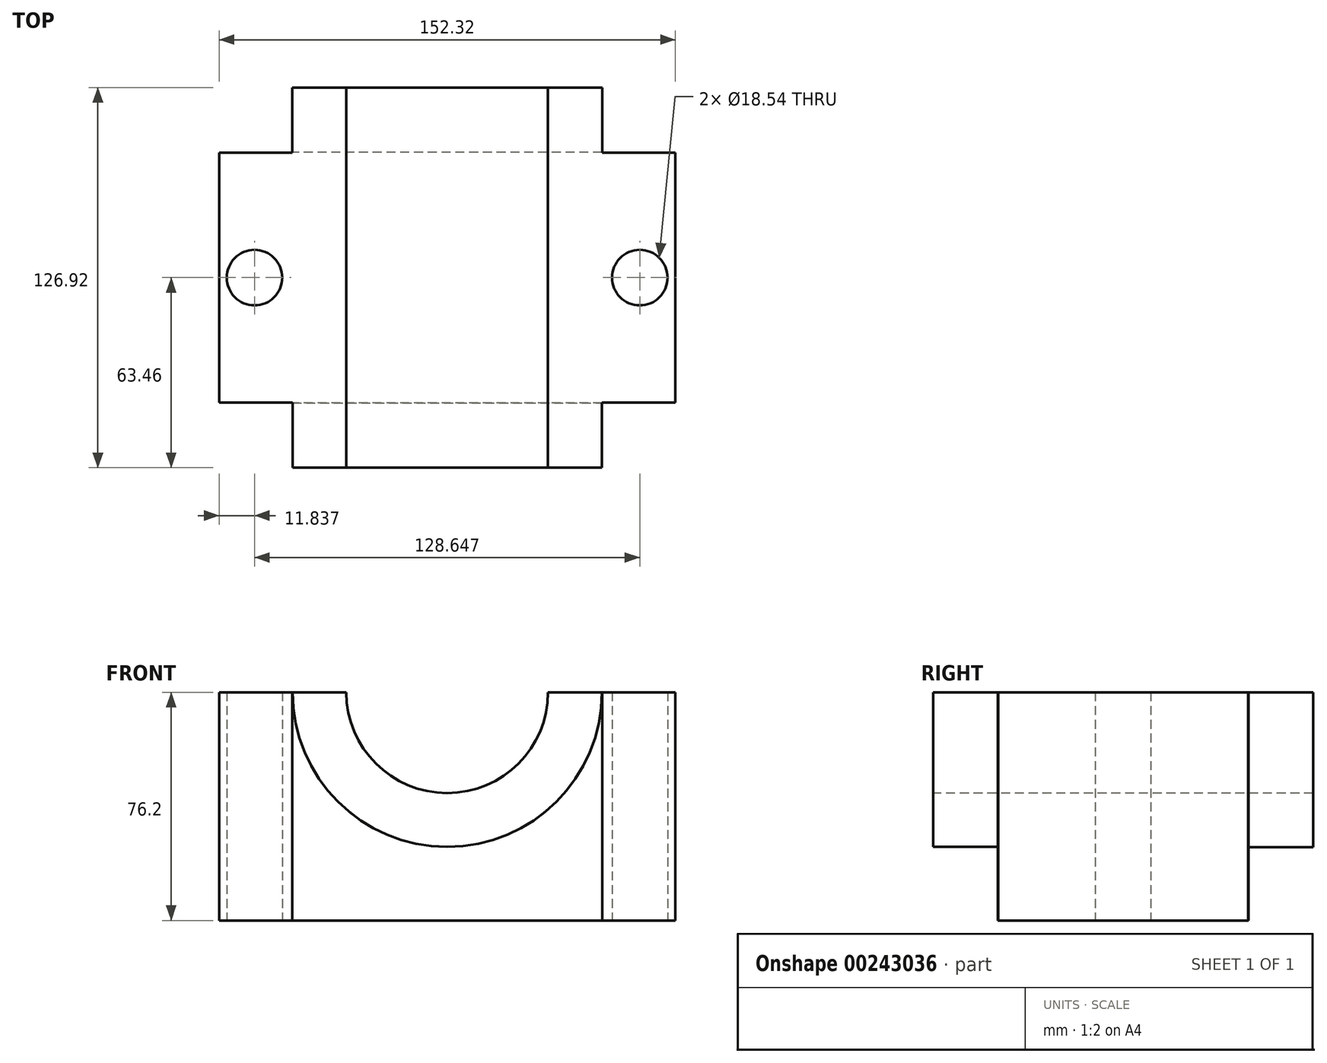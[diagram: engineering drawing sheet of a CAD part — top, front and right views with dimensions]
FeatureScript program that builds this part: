
annotation { "Feature Type Name" : "Feature", "Feature Type Description" : "" }
export const myFeature = defineFeature(function(context is Context, id is Id, definition is map)
    precondition{}
    {
        {
            var Q0;
            Q0=qCreatedBy(makeId("Top.planeOp"),FACE);
            var sketch = newSketch(context, id + "F0", { "sketchPlane" : qUnion([Q0])});
            skLineSegment(sketch, "E0.bottom", {"start": v(76.16, 41.7) * mm, "end": v(-76.16, 41.7) * mm});
            skLineSegment(sketch, "E0.top", {"start": v(76.16, -41.7) * mm, "end": v(-76.16, -41.7) * mm});
            skLineSegment(sketch, "E0.left", {"start": v(76.16, 41.7) * mm, "end": v(76.16, -41.7) * mm});
            skLineSegment(sketch, "E0.right", {"start": v(-76.16, 41.7) * mm, "end": v(-76.16, -41.7) * mm});
            skLineSegment(sketch, "E1.bottom", {"start": v(51.73, 63.46) * mm, "end": v(-51.73, 63.46) * mm});
            skLineSegment(sketch, "E1.top", {"start": v(51.73, -63.46) * mm, "end": v(-51.73, -63.46) * mm});
            skLineSegment(sketch, "E1.left", {"start": v(51.73, 63.46) * mm, "end": v(51.73, -63.46) * mm});
            skLineSegment(sketch, "E1.right", {"start": v(-51.73, 63.46) * mm, "end": v(-51.73, -63.46) * mm});
            skCircle(sketch, "E2", {"center": v(-64.32, 0) * mm, "radius": 9.27 * mm});
            skCircle(sketch, "E3", {"center": v(64.32, 0) * mm, "radius": 9.27 * mm});
            skSolve(sketch);
        }
        {
            var Q0;
            Q0 = qSketchRegion(id + "F0", true);
            extrude(context, id + "F1", {"entities" : qUnion([Q0]), "depth" : 76.2 * mm});
        }
        {
            var Q0;
            Q0=makeQuery(id+"F1.opExtrude","SWEPT_FACE",FACE,{"disambiguationData":[OSD([sQuery(id+"F0.wireOp",EDGE,"E1.top")])]});
            var sketch = newSketch(context, id + "F2", { "sketchPlane" : qUnion([Q0])});
            skArc(sketch, "E4", {"start": v(-51.65, 76.2) * mm, "mid": v(0, 24.55) * mm, "end": v(51.65, 76.2) * mm});
            skArc(sketch, "E5", {"start": v(-33.68, 76.2) * mm, "mid": v(0, 42.52) * mm, "end": v(33.68, 76.2) * mm});
            skLineSegment(sketch, "E6", {"start": v(-51.73, 76.2) * mm, "end": v(51.73, 76.2) * mm});
            skSolve(sketch);
        }
        {
            var Q0;
            {var subQ0=sQuery(id+"F2.wireOp",EDGE,"E5");Q0=makeQuery(id+"F2.imprint","IMPRINT",FACE,{"disambiguationData":[TD([[makeQuery(id+"F2.imprint","IMPRINT",EDGE,{"derivedFrom":subQ0}),1.0]])]});}
            extrude(context, id + "F3", {"entities" : qUnion([Q0]), "operationType" : NewBodyOperationType.REMOVE, "oppositeDirection" : true, "depth" : 172.97 * mm});
        }
        {
            var Q0;
            {var subQ4=sQuery(id+"F2.wireOp",EDGE,"E4");Q0=makeQuery(id+"F2.imprint","IMPRINT",FACE,{"disambiguationData":[TD([[makeQuery(id+"F2.imprint","IMPRINT",EDGE,{"derivedFrom":subQ4}),-1.0]])]});}
            extrude(context, id + "F4", {"entities" : qUnion([Q0]), "operationType" : NewBodyOperationType.REMOVE, "oppositeDirection" : true, "depth" : 21.59 * mm});
        }
        {
            var Q0;
            Q0=makeQuery(id+"F1.opExtrude","SWEPT_FACE",FACE,{"disambiguationData":[OSD([sQuery(id+"F0.wireOp",EDGE,"E1.bottom")])]});
            var sketch = newSketch(context, id + "F5", { "sketchPlane" : qUnion([Q0])});
            skArc(sketch, "E7", {"start": v(-51.73, 76.2) * mm, "mid": v(0, 24.47) * mm, "end": v(51.73, 76.2) * mm});
            skLineSegment(sketch, "E8", {"start": v(-51.73, 76.2) * mm, "end": v(51.73, 76.2) * mm});
            skSolve(sketch);
        }
        {
            var Q0;
            Q0=makeQuery(id+"F5.imprint","IMPRINT",FACE,{"disambiguationData":[TD([[makeQuery(id+"F5.imprint","IMPRINT",EDGE,{"derivedFrom":sQuery(id+"F5.wireOp",EDGE,"E7")}),-1.0]])]});
            extrude(context, id + "F6", {"entities" : qUnion([Q0]), "operationType" : NewBodyOperationType.REMOVE, "oppositeDirection" : true, "depth" : 21.59 * mm});
        }
    });
